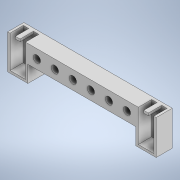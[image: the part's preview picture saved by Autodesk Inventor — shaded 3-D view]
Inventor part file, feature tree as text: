
AUTODESK INVENTOR PART (.ipt)
format: ipt  version: 2020 (Build 240168000, 168)  size: 308,736 bytes
history: native  units: in
note: dims shown in document units (in); Inventor stores cm internally (conversion verified against a paired STEP export)
features: extrude x6, sketch x6
ambient origin geometry x8: Origin, YZ Plane, XZ Plane, XY Plane, X Axis, Y Axis, Z Axis, Center Point
bodies: Solid1 (feature_tree)
feature tree (12):
  extrude  "Extrusion1"  Depth=0.5in
  extrude  "Extrusion2"  Depth=3.0in
  extrude  "Extrusion3"  Depth=0.4487in
  extrude  "Extrusion4"  Depth=0.43in
  extrude  "Extrusion5"  Depth=0.0657in
  extrude  "Extrusion6"  Depth=0.0657in
  sketch  "Sketch1"  dims[d0=0.5615in d1=0.5in]
  sketch  "Sketch2"  dims[d2=0.9615in d3=3.0in]
  sketch  "Sketch3"  dims[d4=1.5in d5=0.4487in]
  sketch  "Sketch5"  dims[d6=0.0in d7=0.43in]
  sketch  "Sketch6"  dims[d8=0.83in d9=0.0657in]
  sketch  "Sketch7"  dims[d10=0.0657in d11=0.0657in d12=0.13in d13=0.37in d14=0.0in d15=0.203in d16=0.25in d17=1.25in d19=0.0in d20=0.0in d21=2.3622in d23=0.5in d24=0.3937in d26=1.0in d28=0.3907in d29=2.3622in d31=0.5in d32=0.3937in d34=1.0in d36=0.125in d37=0.0in d38=2.3622in d40=0.5in d41=0.3937in d43=1.0in d45=0.0079in d46=0.0in d47=2.3622in d49=0.5in d50=0.3937in d52=1.0in d54=0.0079in d55=0.0in]
